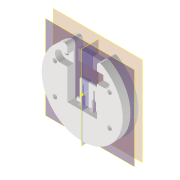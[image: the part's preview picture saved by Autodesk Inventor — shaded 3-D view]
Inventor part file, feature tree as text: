
AUTODESK INVENTOR PART (.ipt)
format: ipt  version: 2022 (Build 260153000, 153)  size: 281,600 bytes
history: native  units: in
note: dims shown in document units (in); Inventor stores cm internally (conversion verified against a paired STEP export)
features: reference x26, sketch x11, extrude x9, other x9, projected_geometry x6, plane x4, fillet x1, hole x1
ambient origin geometry x8: Origin, YZ Plane, XZ Plane, XY Plane, X Axis, Y Axis, Z Axis, Center Point
bodies: Solid1 (feature_tree)
feature tree (67):
  plane  "Work Plane1"
  extrude  "Extrusion1"  Depth=0.3937in
  other  "Arbeitspunkt1"
  plane  "Arbeitsebene4"
  extrude  "Extrusion16"  Depth=0.3937in TaperAngle=0.0deg
  extrude  "Extrusion17"  Depth=0.0394in TaperAngle=0.0deg
  extrude  "Extrusion18"  Depth=0.1181in
  extrude  "Extrusion19"  Depth=0.1181in
  extrude  "Extrusion20"  Depth=0.5512in
  extrude  "Extrusion21"  Depth=0.1575in TaperAngle=0.0deg
  extrude  "Extrusion22"  Depth=0.1102in
  fillet  "Rundung3"  Radius=0.1102in
  plane  "Arbeitsebene5"
  sketch  "Skizze29"  dims[d104=0.0in d105=0.0in d106=0.0787in]
  hole  "Bohrung2"  [1 undecoded]
  plane  "Arbeitsebene6"
  extrude  "Extrusion24"  Depth=0.0787in
  sketch  "Sketch1"  dims[d0=0.3937in d1=0.0in d17=0.7874in]
  reference  "Reference1"
  reference  "Reference5"
  reference  "Reference6"
  reference  "Reference7"
  other  "Arbeitsachse2"
  sketch  "Skizze22"  dims[d82=0.748in d84=0.3937in d85=0.0in]
  projected_geometry  "Projizierte Kontur12"
  sketch  "Skizze23"  dims[d86=0.0669in d87=0.0in d88=0.0394in d89=0.0in]
  sketch  "Skizze24"  dims[d90=0.1181in d91=0.1181in]
  sketch  "Skizze25"  dims[d92=0.1181in d93=0.1181in]
  sketch  "Skizze26"  dims[d94=0.0in d95=0.0in d96=0.5512in]
  projected_geometry  "Projizierte Kontur13"
  sketch  "Skizze27"  dims[d97=0.2756in d98=0.1575in d99=0.0in]
  projected_geometry  "Projizierte Kontur14"
  projected_geometry  "Projizierte Kontur15"
  sketch  "Skizze28"  dims[d100=0.1181in d101=0.0in d102=0.1102in d103=0.1102in]
  projected_geometry  "Projizierte Kontur16"
  sketch  "Skizze30"  dims[d107=0.1142in d108=0.2362in d109=0.1575in d110=0.0787in d111=90.0deg d112=0.2756in d113=0.8108in d116=0.0787in]
  reference  "Referenz27"
  reference  "Referenz28"
  reference  "Referenz29"
  reference  "Referenz30"
  reference  "Referenz31"
  reference  "Referenz32"
  reference  "Referenz33"
  reference  "Referenz34"
  reference  "Referenz35"
  reference  "Referenz36"
  reference  "Referenz37"
  reference  "Referenz38"
  reference  "Referenz39"
  reference  "Referenz40"
  reference  "Referenz41"
  reference  "Referenz42"
  reference  "Referenz43"
  reference  "Referenz44"
  reference  "Referenz45"
  reference  "Referenz46"
  reference  "Referenz47"
  reference  "Referenz48"
  sketch  "Skizze32"  dims[d117=0.2756in d118=0.0in]
  projected_geometry  "Projizierte Kontur18"
  other  "<userpath>\Documents\Matchboxscope\INVENTOR\Matchboxscope_v1.iam"
  other  "Matchboxscope_v1.iam"
  other  "Matchboxscope_middle2_v1:1"
  other  "Baugruppe1"
  other  "Matchboxscope_middle2_v2:1"
  other  "Assembly_USB_Lampassembly.iam"
  other  "USB_dupont_Adapter:1"
note: 1 required parameter value undecoded (feature->parameter linkage not recoverable at this tier; creation-order binding heuristic only, values carry confidence <= 0.55)
